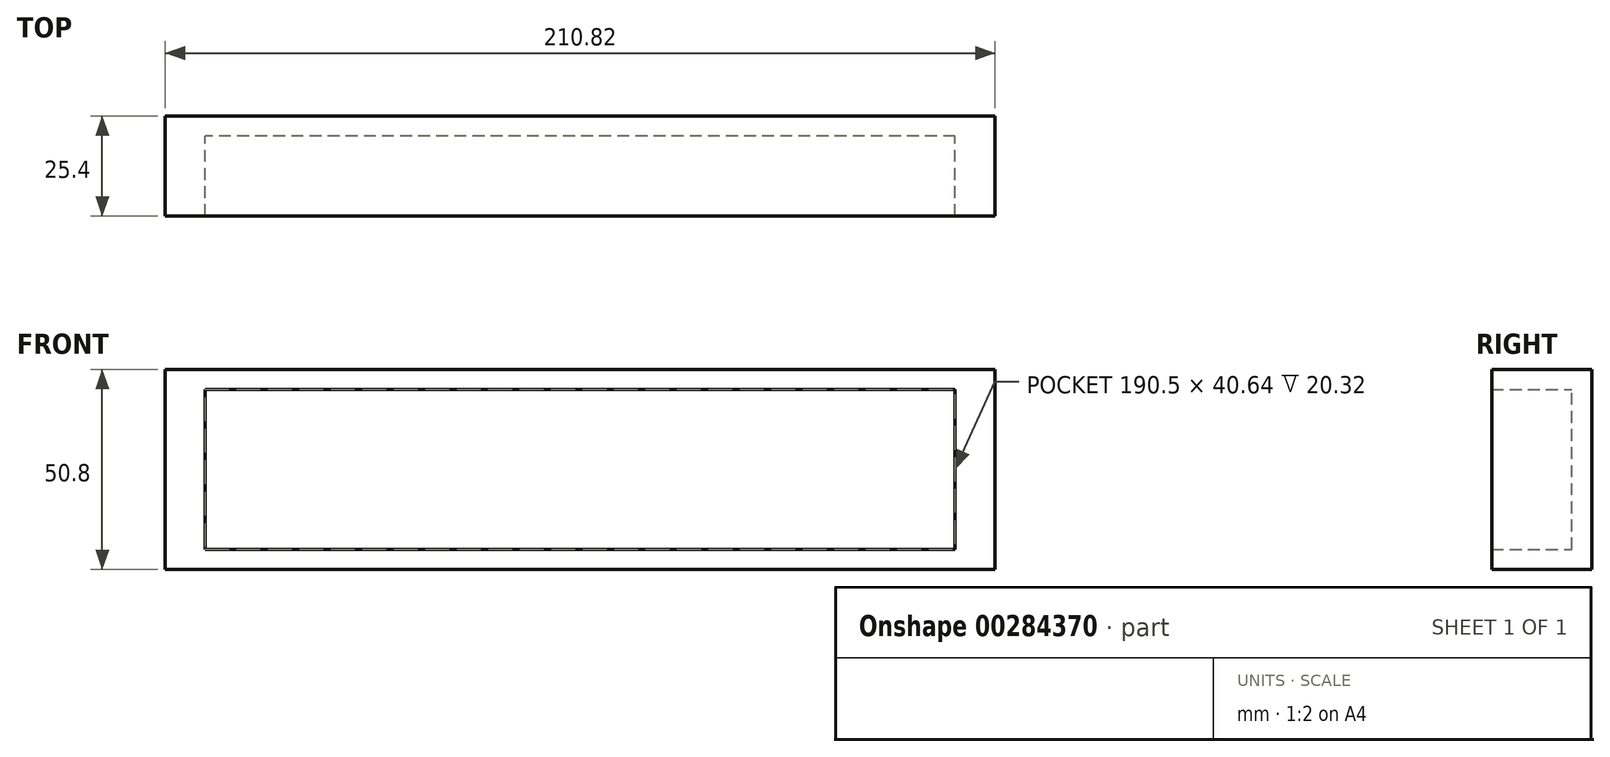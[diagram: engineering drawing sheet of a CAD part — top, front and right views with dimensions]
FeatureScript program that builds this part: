
annotation { "Feature Type Name" : "Feature", "Feature Type Description" : "" }
export const myFeature = defineFeature(function(context is Context, id is Id, definition is map)
    precondition{}
    {
        {
            var Q0;
            Q0=qCreatedBy(makeId("Front.planeOp"),FACE);
            var sketch = newSketch(context, id + "F0", { "sketchPlane" : qUnion([Q0])});
            skLineSegment(sketch, "E0.bottom", {"start": v(95.25, -20.32) * mm, "end": v(-95.25, -20.32) * mm});
            skLineSegment(sketch, "E0.top", {"start": v(95.25, 20.32) * mm, "end": v(-95.25, 20.32) * mm});
            skLineSegment(sketch, "E0.left", {"start": v(95.25, -20.32) * mm, "end": v(95.25, 20.32) * mm});
            skLineSegment(sketch, "E0.right", {"start": v(-95.25, -20.32) * mm, "end": v(-95.25, 20.32) * mm});
            skPoint(sketch, "E0.middle", {"position": v(0, 0) * mm});
            skLineSegment(sketch, "E1", {"start": v(-95.25, -20.32) * mm, "end": v(-95.25, -25.4) * mm});
            skLineSegment(sketch, "E2", {"start": v(-95.25, -25.4) * mm, "end": v(95.25, -25.4) * mm});
            skLineSegment(sketch, "E3", {"start": v(95.25, -20.32) * mm, "end": v(95.25, -25.4) * mm});
            skLineSegment(sketch, "E4", {"start": v(-95.25, 20.32) * mm, "end": v(-95.25, 25.4) * mm});
            skLineSegment(sketch, "E5", {"start": v(-95.25, 25.4) * mm, "end": v(95.25, 25.4) * mm});
            skLineSegment(sketch, "E6", {"start": v(95.25, 25.4) * mm, "end": v(95.25, 20.32) * mm});
            skLineSegment(sketch, "E7", {"start": v(-95.25, 25.4) * mm, "end": v(-105.4, 25.4) * mm});
            skLineSegment(sketch, "E8", {"start": v(-105.4, -25.4) * mm, "end": v(-105.4, 25.4) * mm});
            skLineSegment(sketch, "E9", {"start": v(-95.25, -25.4) * mm, "end": v(-105.4, -25.4) * mm});
            skLineSegment(sketch, "E10", {"start": v(95.25, 25.4) * mm, "end": v(105.41, 25.4) * mm});
            skLineSegment(sketch, "E11", {"start": v(105.41, 25.4) * mm, "end": v(105.41, -25.4) * mm});
            skLineSegment(sketch, "E12", {"start": v(105.41, -25.4) * mm, "end": v(95.25, -25.4) * mm});
            skSolve(sketch);
        }
        {
            var Q0;
            Q0=makeQuery(id+"F0.imprint","IMPRINT",FACE,{"disambiguationData":[TD([[makeQuery(id+"F0.imprint","IMPRINT",EDGE,{"derivedFrom":sQuery(id+"F0.wireOp",EDGE,"E0.bottom")}),-1.0]])]});
            extrude(context, id + "F1", {"entities" : qUnion([Q0]), "depth" : 5.08 * mm});
        }
        {
            var Q0;
            Q0=makeQuery(id+"F0.imprint","IMPRINT",FACE,{"disambiguationData":[TD([[makeQuery(id+"F0.imprint","IMPRINT",EDGE,{"derivedFrom":sQuery(id+"F0.wireOp",EDGE,"E0.right")}),1.0]])]});
            var Q1;
            Q1=makeQuery(id+"F0.imprint","IMPRINT",FACE,{"disambiguationData":[TD([[makeQuery(id+"F0.imprint","IMPRINT",EDGE,{"derivedFrom":sQuery(id+"F0.wireOp",EDGE,"E0.left")}),-1.0]])]});
            var Q2;
            Q2=makeQuery(id+"F0.imprint","IMPRINT",FACE,{"disambiguationData":[TD([[makeQuery(id+"F0.imprint","IMPRINT",EDGE,{"derivedFrom":sQuery(id+"F0.wireOp",EDGE,"E0.bottom")}),1.0]])]});
            var Q3;
            Q3=makeQuery(id+"F0.imprint","IMPRINT",FACE,{"disambiguationData":[TD([[makeQuery(id+"F0.imprint","IMPRINT",EDGE,{"derivedFrom":sQuery(id+"F0.wireOp",EDGE,"E0.top")}),-1.0]])]});
            extrude(context, id + "F2", {"entities" : qUnion([Q0, Q1, Q2, Q3]), "operationType" : NewBodyOperationType.ADD, "depth" : 25.4 * mm});
        }
    });
